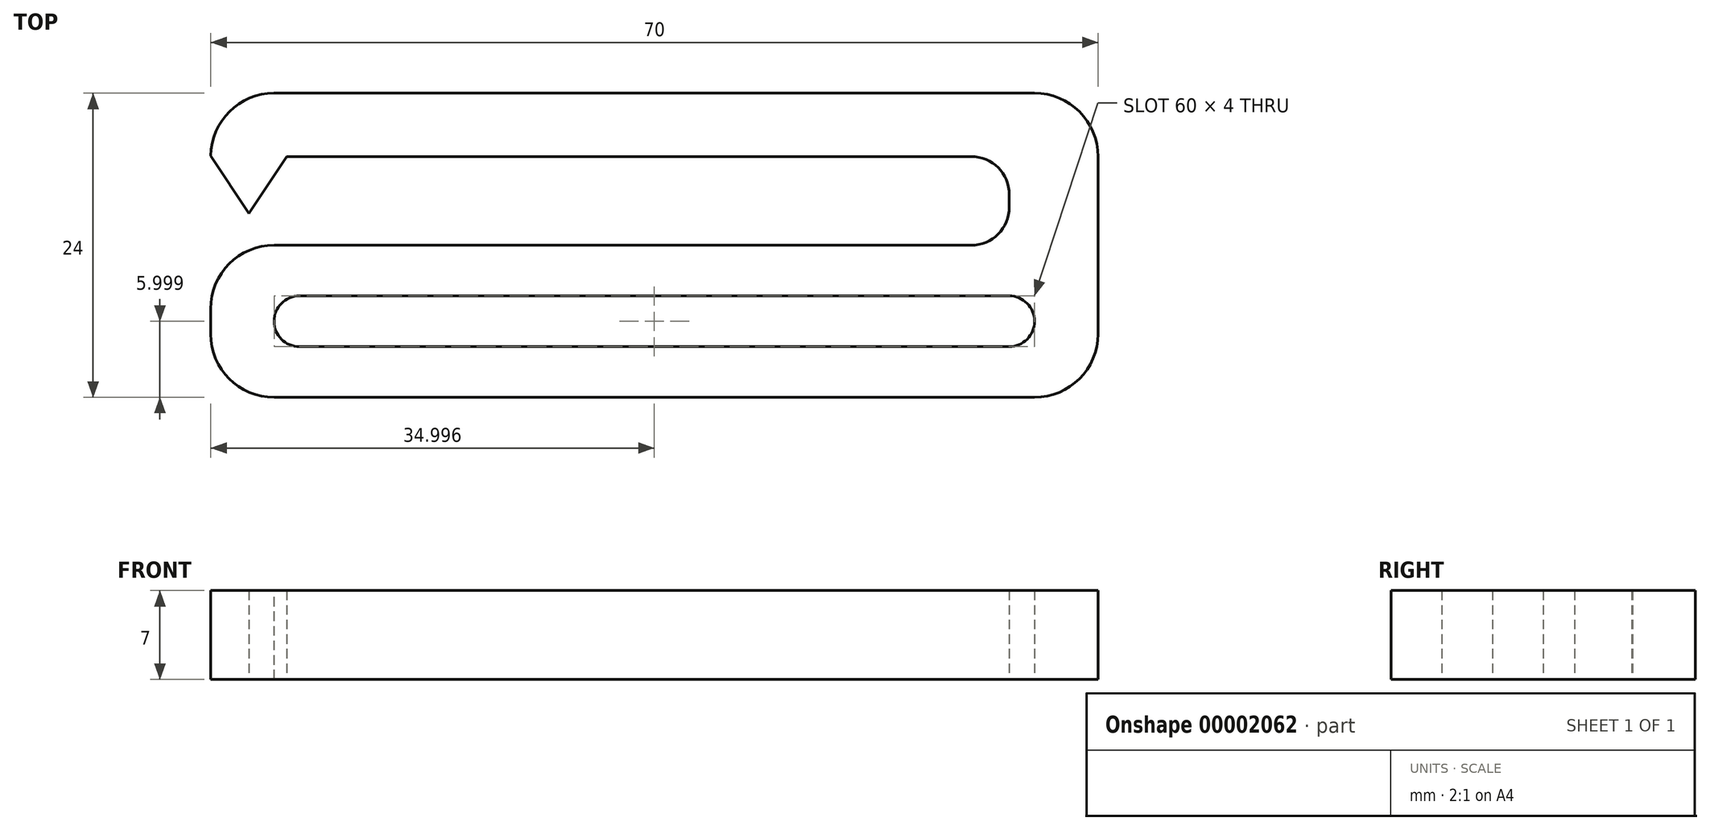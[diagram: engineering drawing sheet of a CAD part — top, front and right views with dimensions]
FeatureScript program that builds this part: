
annotation { "Feature Type Name" : "Feature", "Feature Type Description" : "" }
export const myFeature = defineFeature(function(context is Context, id is Id, definition is map)
    precondition{}
    {
        {
            var Q0;
            Q0=qCreatedBy(makeId("Top.planeOp"),FACE);
            var sketch = newSketch(context, id + "F0", { "sketchPlane" : qUnion([Q0])});
            skLineSegment(sketch, "E0", {"start": v(30.63, -16.46) * mm, "end": v(30.63, 7.54) * mm});
            skLineSegment(sketch, "E1", {"start": v(30.63, 7.54) * mm, "end": v(-39.37, 7.54) * mm});
            skLineSegment(sketch, "E2", {"start": v(-39.37, 7.54) * mm, "end": v(-39.37, 2.6) * mm});
            skLineSegment(sketch, "E3", {"start": v(-39.37, 2.6) * mm, "end": v(-36.37, -1.96) * mm});
            skLineSegment(sketch, "E4", {"start": v(-36.37, -1.96) * mm, "end": v(-33.37, 2.54) * mm});
            skLineSegment(sketch, "E5", {"start": v(-33.37, 2.54) * mm, "end": v(23.63, 2.54) * mm});
            skLineSegment(sketch, "E6", {"start": v(23.63, 2.54) * mm, "end": v(23.63, -4.46) * mm});
            skLineSegment(sketch, "E7", {"start": v(23.63, -4.46) * mm, "end": v(-39.37, -4.46) * mm});
            skLineSegment(sketch, "E8", {"start": v(-39.37, -4.46) * mm, "end": v(-39.37, -16.46) * mm});
            skLineSegment(sketch, "E9", {"start": v(-39.37, -16.46) * mm, "end": v(30.63, -16.46) * mm});
            skLineSegment(sketch, "E10.bottom", {"start": v(-34.37, -8.46) * mm, "end": v(25.63, -8.46) * mm});
            skLineSegment(sketch, "E10.top", {"start": v(-34.37, -12.46) * mm, "end": v(25.63, -12.46) * mm});
            skLineSegment(sketch, "E10.left", {"start": v(-34.37, -8.46) * mm, "end": v(-34.37, -12.46) * mm});
            skLineSegment(sketch, "E10.right", {"start": v(25.63, -8.46) * mm, "end": v(25.63, -12.46) * mm});
            skSolve(sketch);
        }
        {
            var Q0;
            Q0 = qSketchRegion(id + "F0", true);
            extrude(context, id + "F1", {"entities" : qUnion([Q0]), "depth" : 7 * mm});
        }
        {
            var Q0;
            Q0=makeQuery(id+"F1.opExtrude","SWEPT_EDGE",EDGE,{"disambiguationData":[OSD([sQuery(id+"F0.wireOp",EDGE,"E10.top"),sQuery(id+"F0.wireOp",EDGE,"E10.left")])]});
            var Q1;
            Q1=makeQuery(id+"F1.opExtrude","SWEPT_EDGE",EDGE,{"disambiguationData":[OSD([sQuery(id+"F0.wireOp",EDGE,"E10.bottom"),sQuery(id+"F0.wireOp",EDGE,"E10.left")])]});
            var Q2;
            Q2=makeQuery(id+"F1.opExtrude","SWEPT_EDGE",EDGE,{"disambiguationData":[OSD([sQuery(id+"F0.wireOp",EDGE,"E10.top"),sQuery(id+"F0.wireOp",EDGE,"E10.right")])]});
            var Q3;
            Q3=makeQuery(id+"F1.opExtrude","SWEPT_EDGE",EDGE,{"disambiguationData":[OSD([sQuery(id+"F0.wireOp",EDGE,"E10.bottom"),sQuery(id+"F0.wireOp",EDGE,"E10.right")])]});
            fillet(context, id + "F2", {"entities" : qUnion([Q0, Q1, Q2, Q3]), "radius" : 2 * mm, "tangentPropagation" : true, "allowEdgeOverflow" : false});
        }
        {
            var Q0;
            Q0=makeQuery(id+"F1.opExtrude","SWEPT_EDGE",EDGE,{"disambiguationData":[OSD([sQuery(id+"F0.wireOp",EDGE,"E1"),sQuery(id+"F0.wireOp",EDGE,"E2")])]});
            var Q1;
            Q1=makeQuery(id+"F1.opExtrude","SWEPT_EDGE",EDGE,{"disambiguationData":[OSD([sQuery(id+"F0.wireOp",EDGE,"E8"),sQuery(id+"F0.wireOp",EDGE,"E9")])]});
            var Q2;
            Q2=makeQuery(id+"F1.opExtrude","SWEPT_EDGE",EDGE,{"disambiguationData":[OSD([sQuery(id+"F0.wireOp",EDGE,"E7"),sQuery(id+"F0.wireOp",EDGE,"E8")])]});
            var Q3;
            Q3=makeQuery(id+"F1.opExtrude","SWEPT_EDGE",EDGE,{"disambiguationData":[OSD([sQuery(id+"F0.wireOp",EDGE,"E0"),sQuery(id+"F0.wireOp",EDGE,"E1")])]});
            var Q4;
            Q4=makeQuery(id+"F1.opExtrude","SWEPT_EDGE",EDGE,{"disambiguationData":[OSD([sQuery(id+"F0.wireOp",EDGE,"E0"),sQuery(id+"F0.wireOp",EDGE,"E9")])]});
            fillet(context, id + "F3", {"entities" : qUnion([Q0, Q1, Q2, Q3, Q4]), "radius" : 5 * mm, "tangentPropagation" : true, "allowEdgeOverflow" : false});
        }
        {
            var Q0;
            Q0=makeQuery(id+"F1.opExtrude","SWEPT_EDGE",EDGE,{"disambiguationData":[OSD([sQuery(id+"F0.wireOp",EDGE,"E6"),sQuery(id+"F0.wireOp",EDGE,"E7")])]});
            var Q1;
            Q1=makeQuery(id+"F1.opExtrude","SWEPT_EDGE",EDGE,{"disambiguationData":[OSD([sQuery(id+"F0.wireOp",EDGE,"E5"),sQuery(id+"F0.wireOp",EDGE,"E6")])]});
            fillet(context, id + "F4", {"entities" : qUnion([Q0, Q1]), "radius" : 3 * mm, "tangentPropagation" : true, "allowEdgeOverflow" : false});
        }
        {
            var Q0;
            Q0=makeQuery(id+"F1.opExtrude","SWEPT_FACE",FACE,{"disambiguationData":[OSD([sQuery(id+"F0.wireOp",EDGE,"E9")])]});
            cPlane(context, id + "F5", {"entities" : qUnion([Q0]), "cplaneType" : CPlaneType.OFFSET, "offset" : 0 * mm, "width" : 150 * mm, "height" : 150 * mm});
        }
    });
